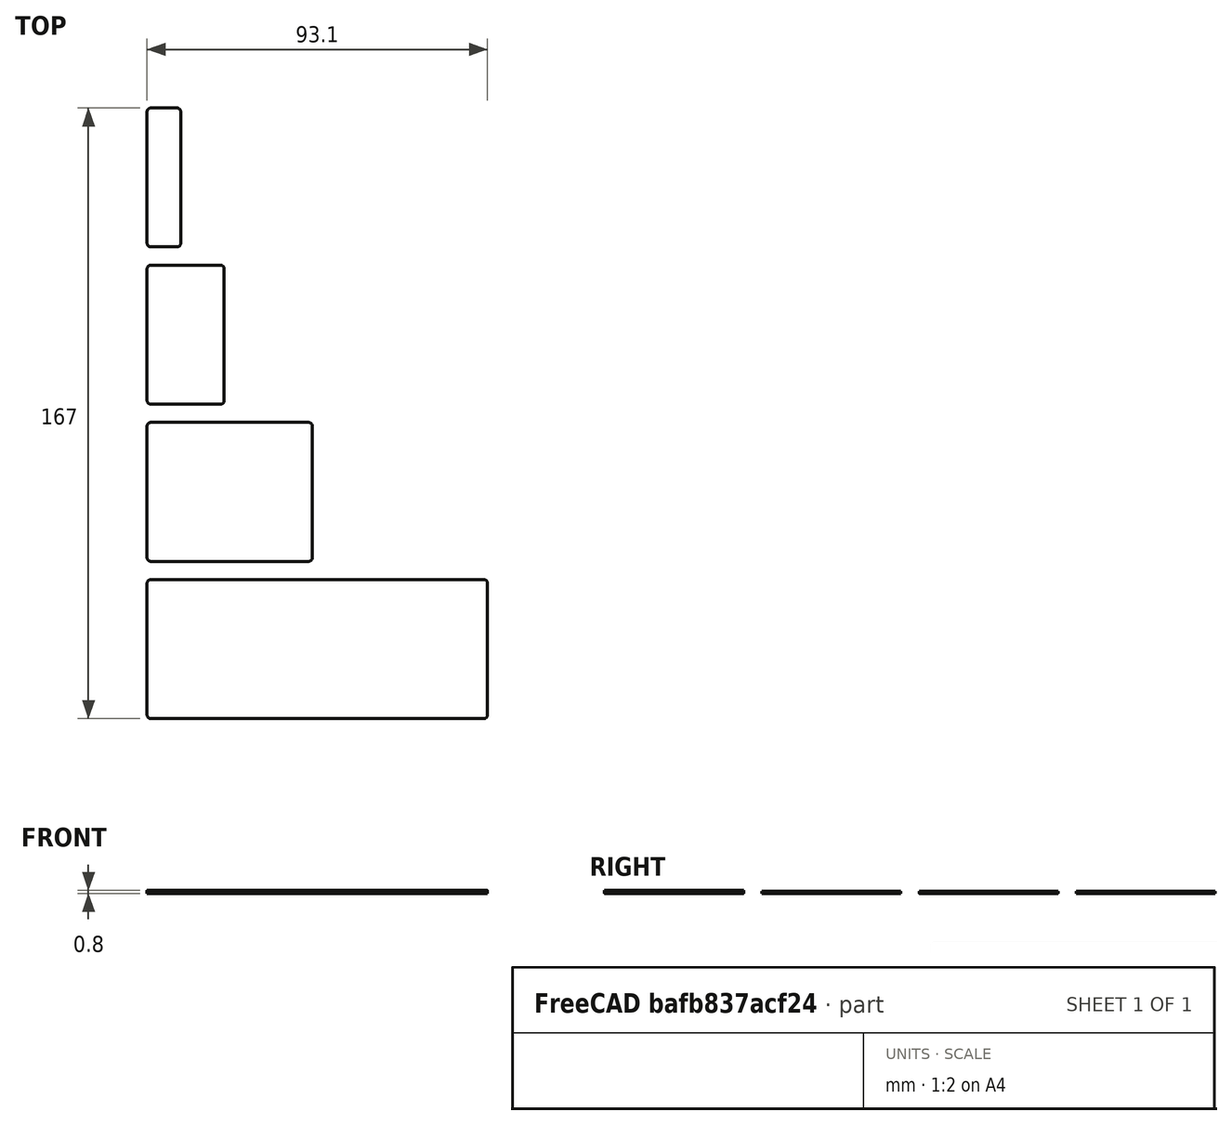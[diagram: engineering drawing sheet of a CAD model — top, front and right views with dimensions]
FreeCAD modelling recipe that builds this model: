
FCSTD DOCUMENT  (FreeCAD 0.16R)
Label: 1story_separators
License: All rights reserved
LicenseURL: http://en.wikipedia.org/wiki/All_rights_reserved
objects: Part::Box×4, Part::Fillet×4
note: 8 computed .brp shape members not serialized (recipe doc carries the construction recipe); baked Part::Feature solids carry a one-line shape summary decoded from their .brp

FEATURE [Part::Box] Box  label="Cube"
  Height = 0.8
  Length = 93.1
  Width = 38
FEATURE [Part::Box] Box001  label="Cube001"
  Height = 0.6
  Length = 45.2
  Width = 38
FEATURE [Part::Fillet] Fillet001  label="StandardSeparator"
  Base = -> Box001
  Edges = 4 edges r=1: [Edge1,Edge3,Edge5,Edge7]
  Placement = pos=(0,43,0) rot=(0,0,1;0rad)
FEATURE [Part::Box] Box002  label="Cube002"
  Height = 0.6
  Length = 21.1
  Width = 38
FEATURE [Part::Fillet] Fillet002  label="SmallSeparator"
  Base = -> Box002
  Edges = 4 edges r=1: [Edge1,Edge3,Edge5,Edge7]
  Placement = pos=(0,86,0) rot=(0,0,1;0rad)
FEATURE [Part::Box] Box003  label="Cube003"
  Height = 0.6
  Length = 9.2
  Width = 38
FEATURE [Part::Fillet] Fillet003  label="TinySeparator"
  Base = -> Box003
  Edges = 4 edges r=1: [Edge1,Edge3,Edge5,Edge7]
  Placement = pos=(0,129,0) rot=(0,0,1;0rad)
FEATURE [Part::Fillet] Fillet  label="BigSeparator"
  Base = -> Box
  Edges = 4 edges r=1: [Edge1,Edge3,Edge5,Edge7]
